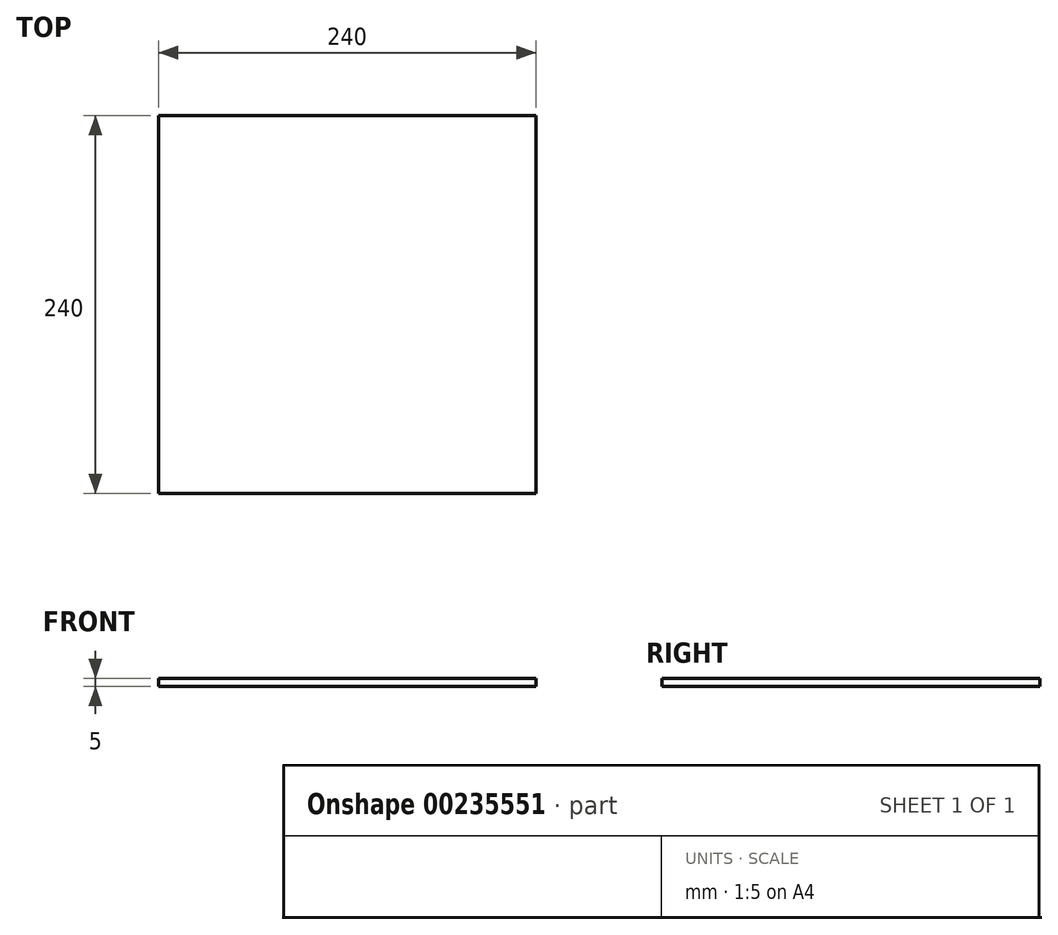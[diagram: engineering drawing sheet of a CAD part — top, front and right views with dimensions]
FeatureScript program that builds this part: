
annotation { "Feature Type Name" : "Feature", "Feature Type Description" : "" }
export const myFeature = defineFeature(function(context is Context, id is Id, definition is map)
    precondition{}
    {
        {
            var Q0;
            Q0=qCreatedBy(makeId("Top.planeOp"),FACE);
            var sketch = newSketch(context, id + "F0", { "sketchPlane" : qUnion([Q0])});
            skLineSegment(sketch, "E0.bottom", {"start": v(120, -120) * mm, "end": v(-120, -120) * mm});
            skLineSegment(sketch, "E0.top", {"start": v(120, 120) * mm, "end": v(-120, 120) * mm});
            skLineSegment(sketch, "E0.left", {"start": v(120, -120) * mm, "end": v(120, 120) * mm});
            skLineSegment(sketch, "E0.right", {"start": v(-120, -120) * mm, "end": v(-120, 120) * mm});
            skPoint(sketch, "E0.middle", {"position": v(0, 0) * mm});
            skSolve(sketch);
        }
        {
            var Q0;
            Q0=makeQuery(id+"F0.imprint","IMPRINT",FACE,{"disambiguationData":[TD([[makeQuery(id+"F0.imprint","IMPRINT",EDGE,{"derivedFrom":sQuery(id+"F0.wireOp",EDGE,"E0.bottom")}),-1.0]])]});
            extrude(context, id + "F1", {"entities" : qUnion([Q0]), "depth" : 5 * mm});
        }
    });
